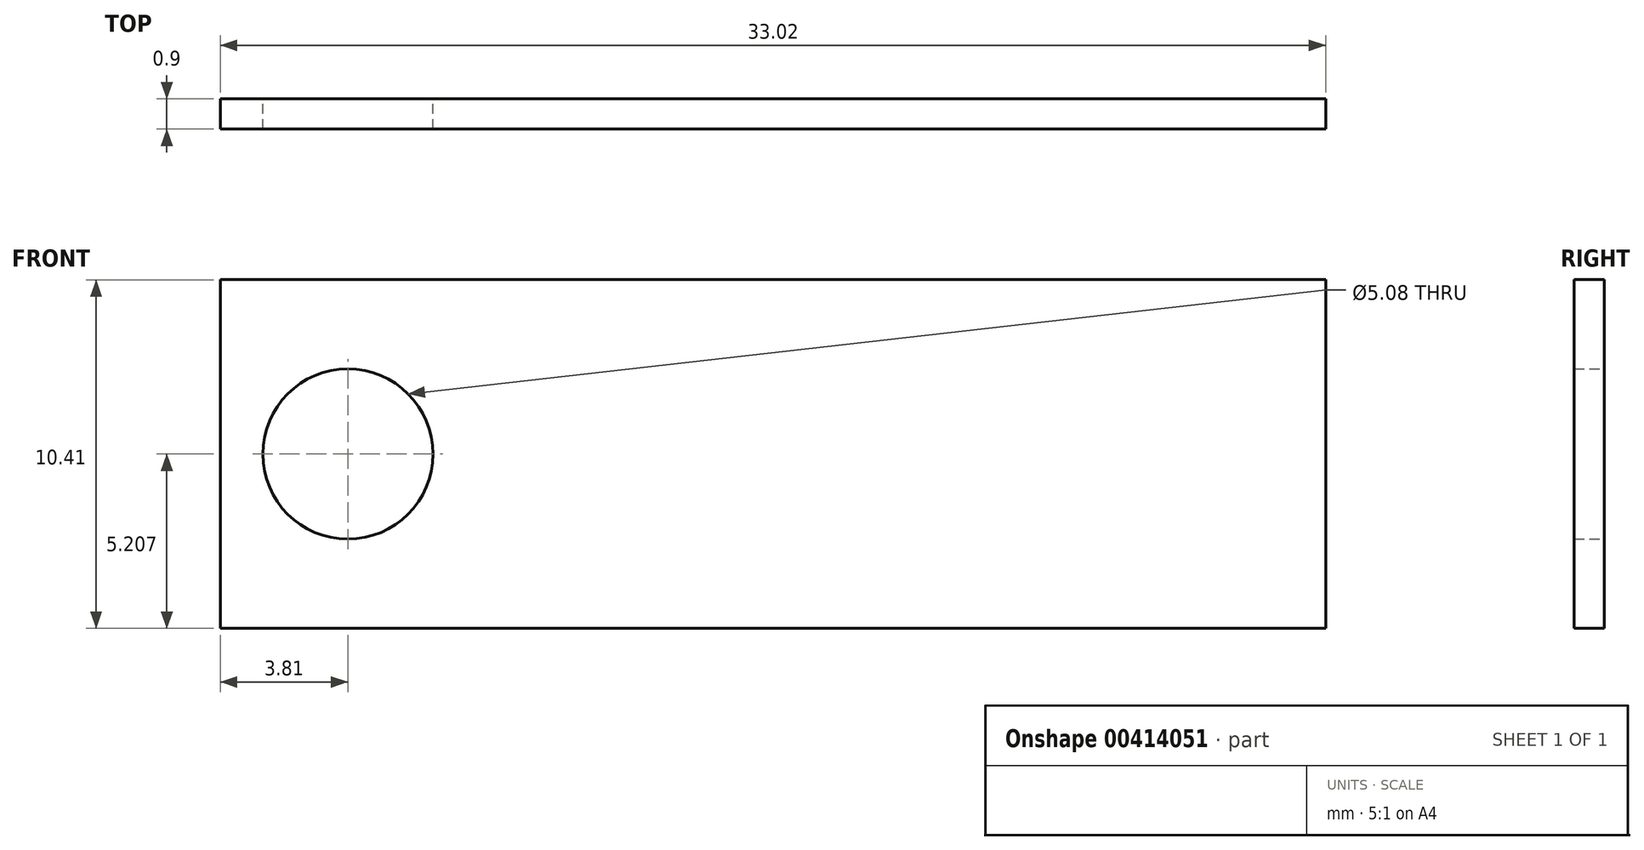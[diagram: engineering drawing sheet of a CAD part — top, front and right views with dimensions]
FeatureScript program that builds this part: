
annotation { "Feature Type Name" : "Feature", "Feature Type Description" : "" }
export const myFeature = defineFeature(function(context is Context, id is Id, definition is map)
    precondition{}
    {
        {
            var Q0;
            Q0=qCreatedBy(makeId("Front.planeOp"),FACE);
            var sketch = newSketch(context, id + "F0", { "sketchPlane" : qUnion([Q0])});
            skLineSegment(sketch, "E0.bottom", {"start": v(0, 0) * mm, "end": v(33.02, 0) * mm});
            skLineSegment(sketch, "E0.top", {"start": v(0, 10.41) * mm, "end": v(33.02, 10.41) * mm});
            skLineSegment(sketch, "E0.left", {"start": v(0, 0) * mm, "end": v(0, 10.41) * mm});
            skLineSegment(sketch, "E0.right", {"start": v(33.02, 0) * mm, "end": v(33.02, 10.41) * mm});
            skCircle(sketch, "E1", {"center": v(3.8, 5.2) * mm, "radius": 2.54 * mm});
            skSolve(sketch);
        }
        {
            var Q0;
            Q0=makeQuery(id+"F0.imprint","IMPRINT",FACE,{"disambiguationData":[TD([[makeQuery(id+"F0.imprint","IMPRINT",EDGE,{"derivedFrom":sQuery(id+"F0.wireOp",EDGE,"E0.bottom")}),1.0]])]});
            extrude(context, id + "F1", {"entities" : qUnion([Q0]), "depth" : .9 * mm});
        }
    });
